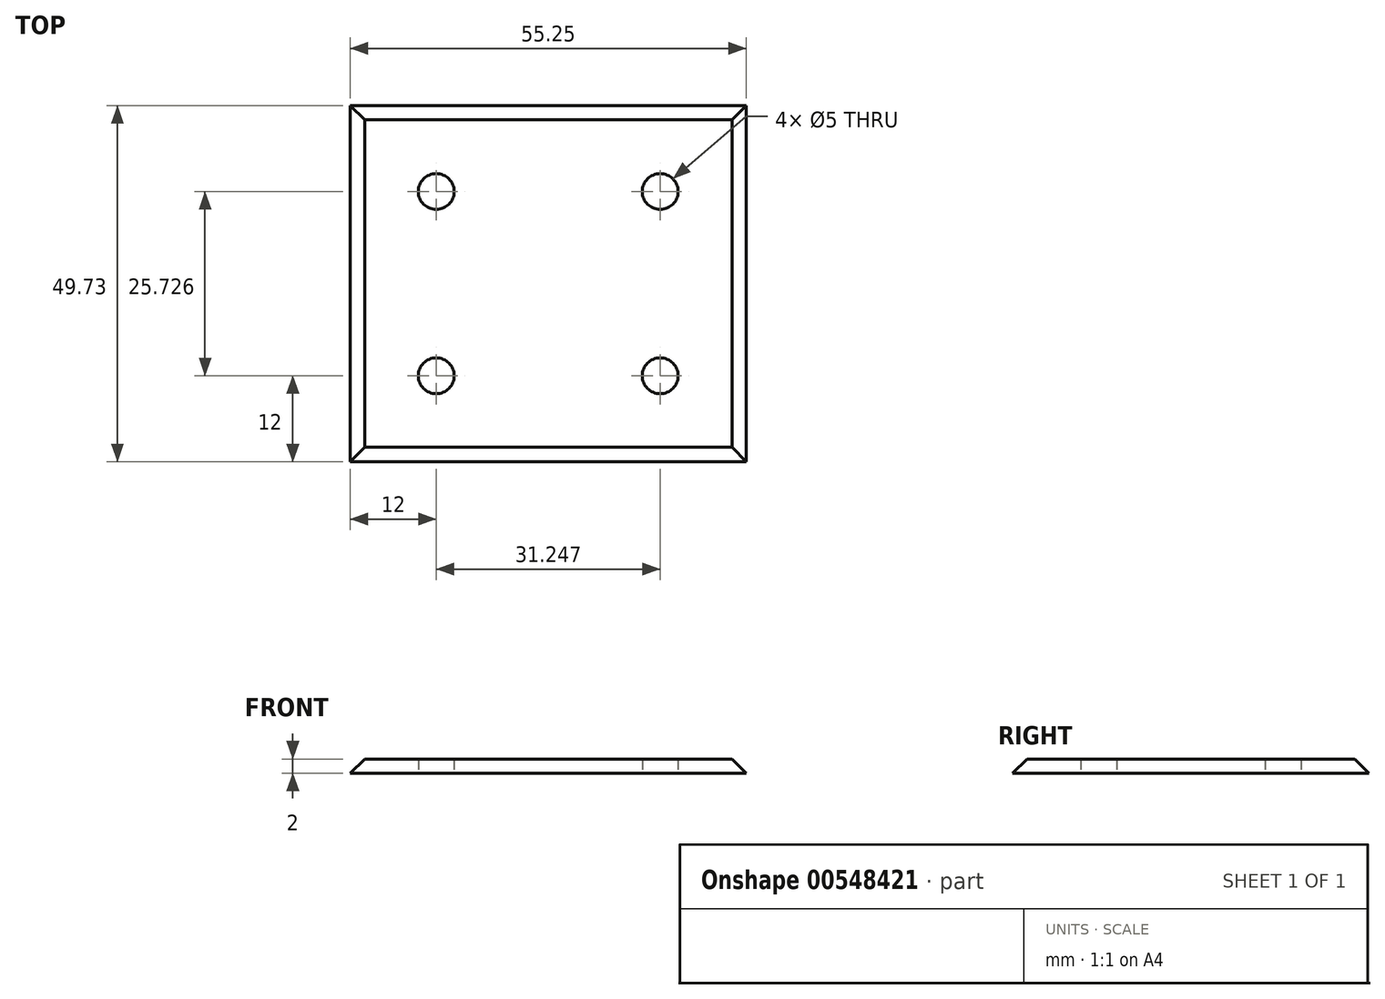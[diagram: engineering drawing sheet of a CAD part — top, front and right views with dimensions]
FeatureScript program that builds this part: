
annotation { "Feature Type Name" : "Feature", "Feature Type Description" : "" }
export const myFeature = defineFeature(function(context is Context, id is Id, definition is map)
    precondition{}
    {
        {
            var Q0;
            Q0=qCreatedBy(makeId("Top.planeOp"),FACE);
            var sketch = newSketch(context, id + "F0", { "sketchPlane" : qUnion([Q0])});
            skLineSegment(sketch, "E0.bottom", {"start": v(0, 0) * mm, "end": v(61.25, 0) * mm});
            skLineSegment(sketch, "E0.top", {"start": v(0, 55.73) * mm, "end": v(61.25, 55.73) * mm});
            skLineSegment(sketch, "E0.left", {"start": v(0, 0) * mm, "end": v(0, 55.73) * mm});
            skLineSegment(sketch, "E0.right", {"start": v(61.25, 0) * mm, "end": v(61.25, 55.73) * mm});
            skSolve(sketch);
        }
        {
            var Q0;
            Q0=makeQuery(id+"F0.imprint","IMPRINT",FACE,{"disambiguationData":[TD([[makeQuery(id+"F0.imprint","IMPRINT",EDGE,{"derivedFrom":sQuery(id+"F0.wireOp",EDGE,"E0.bottom")}),1.0]])]});
            extrude(context, id + "F1", {"entities" : qUnion([Q0]), "depth" : 2 * mm, "offsetDistance" : 25.4 * mm});
        }
        {
            var Q0;
            Q0=makeQuery(id+"F1.opExtrude","CAP_FACE",FACE,{"disambiguationData":[OSD([sQuery(id+"F0.wireOp",EDGE,"E0.bottom"),sQuery(id+"F0.wireOp",EDGE,"E0.top"),sQuery(id+"F0.wireOp",EDGE,"E0.left"),sQuery(id+"F0.wireOp",EDGE,"E0.right")])],"isStart":false});
            var sketch = newSketch(context, id + "F2", { "sketchPlane" : qUnion([Q0])});
            skSolve(sketch);
        }
        {
            var Q0;
            Q0=qCreatedBy(makeId("Top.planeOp"),FACE);
            var sketch = newSketch(context, id + "F3", { "sketchPlane" : qUnion([Q0])});
            skPoint(sketch, "E1", {"position": v(15, 15) * mm});
            skPoint(sketch, "E2", {"position": v(46.25, 15) * mm});
            skPoint(sketch, "E3", {"position": v(46.25, 40.73) * mm});
            skPoint(sketch, "E4", {"position": v(15, 40.73) * mm});
            skSolve(sketch);
        }
        {
            var Q0;
            Q0=sQuery(id+"F3.wireOp",VERTEX,"E4");
            var Q1;
            Q1=sQuery(id+"F3.wireOp",VERTEX,"E3");
            var Q2;
            Q2=sQuery(id+"F3.wireOp",VERTEX,"E1");
            var Q3;
            Q3=sQuery(id+"F3.wireOp",VERTEX,"E2");
            var Q4;
            Q4=makeQuery(id+"F1.opExtrude","SWEPT_BODY",BODY,{"disambiguationData":[OSD([sQuery(id+"F0.wireOp",EDGE,"E0.bottom"),sQuery(id+"F0.wireOp",EDGE,"E0.top"),sQuery(id+"F0.wireOp",EDGE,"E0.left"),sQuery(id+"F0.wireOp",EDGE,"E0.right")])]});
            hole(context, id + "F4", {"style" : HoleStyle.SIMPLE, "endStyle" : HoleEndStyle.THROUGH, "oppositeDirection" : true, "holeDiameter" : 5 * mm, "isTappedThrough" : true, "tappedDepth" : 12 * mm, "tapClearance" : 3, "locations" : qUnion([Q0, Q1, Q2, Q3]), "scope" : qUnion([Q4])});
        }
        {
            var Q0;
            Q0=makeQuery(id+"F1.opExtrude","CAP_EDGE",EDGE,{"disambiguationData":[OSD([sQuery(id+"F0.wireOp",EDGE,"E0.left")])],"isStart":false});
            var Q1;
            Q1=makeQuery(id+"F1.opExtrude","CAP_EDGE",EDGE,{"disambiguationData":[OSD([sQuery(id+"F0.wireOp",EDGE,"E0.top")])],"isStart":false});
            var Q2;
            Q2=makeQuery(id+"F1.opExtrude","CAP_EDGE",EDGE,{"disambiguationData":[OSD([sQuery(id+"F0.wireOp",EDGE,"E0.right")])],"isStart":false});
            var Q3;
            Q3=makeQuery(id+"F1.opExtrude","CAP_EDGE",EDGE,{"disambiguationData":[OSD([sQuery(id+"F0.wireOp",EDGE,"E0.bottom")])],"isStart":false});
            chamfer(context, id + "F5", {"entities" : qUnion([Q0, Q1, Q2, Q3]), "width" : 5 * mm, "tangentPropagation" : true});
        }
    });
